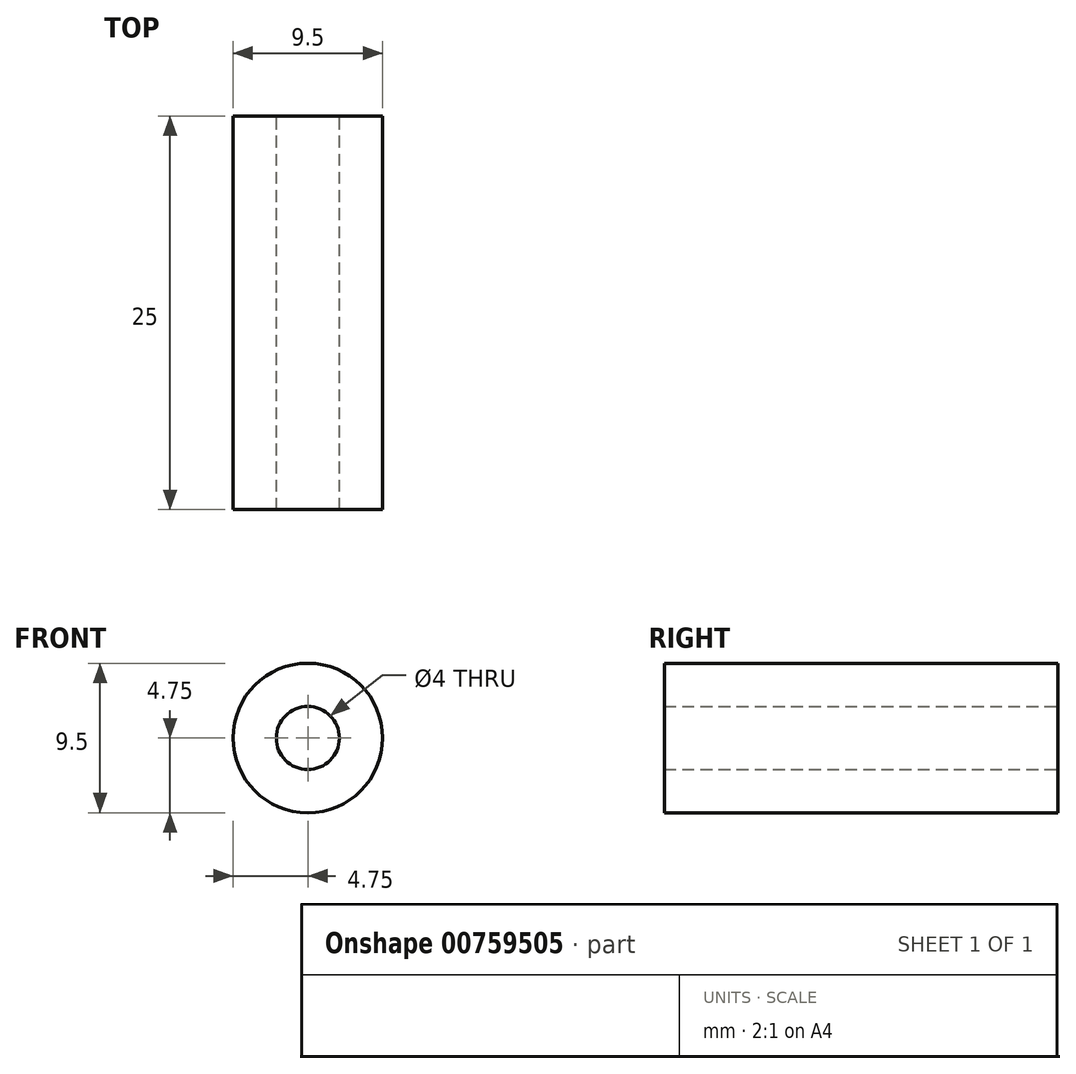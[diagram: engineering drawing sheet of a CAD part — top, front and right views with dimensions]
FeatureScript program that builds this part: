
annotation { "Feature Type Name" : "Feature", "Feature Type Description" : "" }
export const myFeature = defineFeature(function(context is Context, id is Id, definition is map)
    precondition{}
    {
        {
            var Q0;
            Q0=qCreatedBy(makeId("Front.planeOp"),FACE);
            var sketch = newSketch(context, id + "F0", { "sketchPlane" : qUnion([Q0])});
            skCircle(sketch, "E0", {"center": v(0, 0) * mm, "radius": 4.75 * mm});
            skSolve(sketch);
        }
        {
            var Q0;
            Q0=qCreatedBy(makeId("Front.planeOp"),FACE);
            var sketch = newSketch(context, id + "F1", { "sketchPlane" : qUnion([Q0])});
            skCircle(sketch, "E1", {"center": v(0, 0) * mm, "radius": 2 * mm});
            skSolve(sketch);
        }
        {
            var Q0;
            Q0=makeQuery(id+"F0.imprint","IMPRINT",FACE,{"disambiguationData":[TD([[makeQuery(id+"F0.imprint","IMPRINT",EDGE,{"derivedFrom":sQuery(id+"F0.wireOp",EDGE,"E0")}),1.0]])]});
            extrude(context, id + "F2", {"entities" : qUnion([Q0]), "depth" : 25 * mm, "offsetDistance" : 25 * mm});
        }
        {
            var Q0;
            Q0=makeQuery(id+"F1.imprint","IMPRINT",FACE,{"disambiguationData":[TD([[makeQuery(id+"F1.imprint","IMPRINT",EDGE,{"derivedFrom":sQuery(id+"F1.wireOp",EDGE,"E1")}),1.0]])]});
            var Q1;
            Q1=sQuery(id+"F1.wireOp",EDGE,"E1");
            extrude(context, id + "F3", {"entities" : qUnion([Q0]), "operationType" : NewBodyOperationType.REMOVE, "surfaceEntities" : qUnion([Q1]), "depth" : 25 * mm, "offsetDistance" : 25 * mm});
        }
    });
